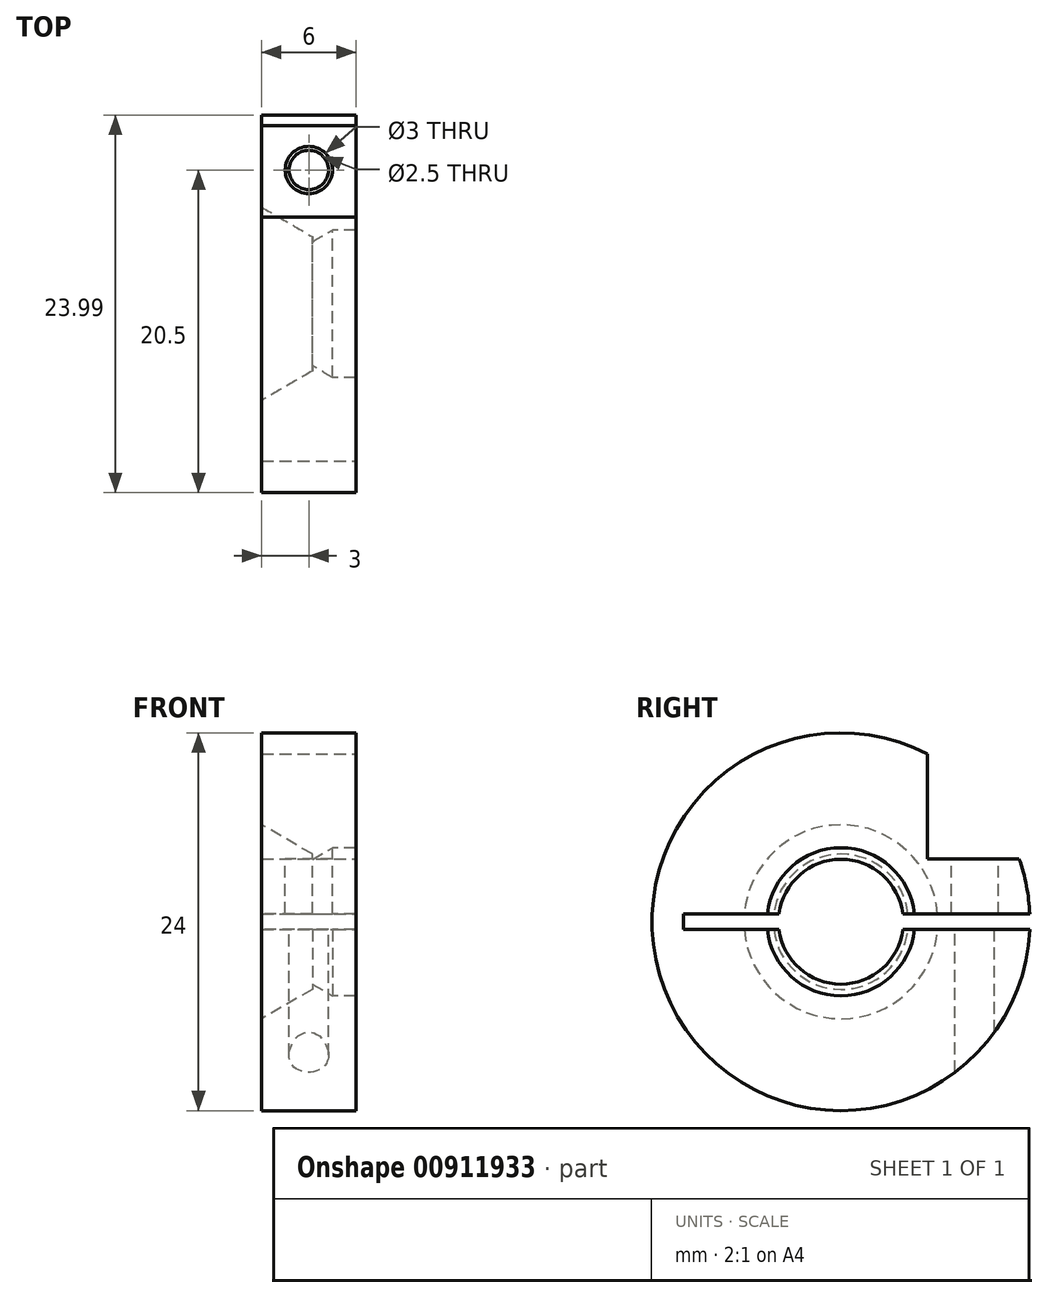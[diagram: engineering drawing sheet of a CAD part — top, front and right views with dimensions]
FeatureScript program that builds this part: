
annotation { "Feature Type Name" : "Feature", "Feature Type Description" : "" }
export const myFeature = defineFeature(function(context is Context, id is Id, definition is map)
    precondition{}
    {
        {
            var Q0;
            Q0=qCreatedBy(makeId("Top.planeOp"),FACE);
            var sketch = newSketch(context, id + "F0", { "sketchPlane" : qUnion([Q0])});
            skCircle(sketch, "E0", {"center": v(0, 8.5) * mm, "radius": 1.5 * mm});
            skCircle(sketch, "E1", {"center": v(0, 8.5) * mm, "radius": 2.8 * mm});
            skLineSegment(sketch, "E2", {"start": v(3, -4.7) * mm, "end": v(3, -12) * mm});
            skLineSegment(sketch, "E3", {"start": v(1.5, -4.7) * mm, "end": v(3, -4.7) * mm});
            skLineSegment(sketch, "E4", {"start": v(1.5, -4.7) * mm, "end": v(0.23, -3.97) * mm});
            skLineSegment(sketch, "E5", {"start": v(-3, -12) * mm, "end": v(3, -12) * mm});
            skLineSegment(sketch, "E6", {"start": v(-3, -6.16) * mm, "end": v(-3, -12) * mm});
            skLineSegment(sketch, "E7", {"start": v(0.23, -4.3) * mm, "end": v(-3, -6.16) * mm});
            skLineSegment(sketch, "E8", {"start": v(0.23, -3.97) * mm, "end": v(0.23, -4.3) * mm});
            skLineSegment(sketch, "E9", {"start": v(1.5, 4.7) * mm, "end": v(3, 4.7) * mm});
            skLineSegment(sketch, "E10", {"start": v(1.5, 4.7) * mm, "end": v(0.23, 3.97) * mm});
            skLineSegment(sketch, "E11", {"start": v(-3, 12) * mm, "end": v(3, 12) * mm});
            skLineSegment(sketch, "E12", {"start": v(0.23, 4.3) * mm, "end": v(-3, 6.16) * mm});
            skLineSegment(sketch, "E13", {"start": v(-3, 6.16) * mm, "end": v(-3, 12) * mm});
            skLineSegment(sketch, "E14", {"start": v(0.23, 3.97) * mm, "end": v(0.23, 4.3) * mm});
            skLineSegment(sketch, "E15", {"start": v(3, 4.7) * mm, "end": v(3, 12) * mm});
            skLineSegment(sketch, "E16", {"start": v(-14.26, 0) * mm, "end": v(18.11, 0) * mm, "construction": true});
            skSolve(sketch);
        }
        {
            var Q0;
            Q0=makeQuery(id+"F0.imprint","IMPRINT",FACE,{"disambiguationData":[TD([[makeQuery(id+"F0.imprint","IMPRINT",EDGE,{"derivedFrom":sQuery(id+"F0.wireOp",EDGE,"E2")}),-1.0]])]});
            var Q1;
            Q1=sQuery(id+"F0.wireOp",EDGE,"E16");
            revolve(context, id + "F1", {"surfaceOperationType" : NewSurfaceOperationType.NEW, "entities" : qUnion([Q0]), "axis" : qUnion([Q1]), "revolveType" : RevolveType.FULL});
        }
        {
            var Q0;
            Q0=makeQuery(id+"F1.opRevolve","SWEPT_FACE",FACE,{"disambiguationData":[OSD([sQuery(id+"F0.wireOp",EDGE,"E2")])]});
            var sketch = newSketch(context, id + "F2", { "sketchPlane" : qUnion([Q0])});
            skLineSegment(sketch, "E17", {"start": v(0, 12) * mm, "end": v(0, 0) * mm, "construction": true});
            skLineSegment(sketch, "E18", {"start": v(0, 0) * mm, "end": v(12, 0) * mm, "construction": true});
            skLineSegment(sketch, "E19", {"start": v(5.5, 10.67) * mm, "end": v(5.5, 4) * mm});
            skLineSegment(sketch, "E20", {"start": v(5.5, 4) * mm, "end": v(11.31, 4) * mm});
            skLineSegment(sketch, "E21", {"start": v(-10, 0.5) * mm, "end": v(13, 0.5) * mm});
            skLineSegment(sketch, "E22", {"start": v(13, 0.5) * mm, "end": v(13, -0.5) * mm});
            skLineSegment(sketch, "E23", {"start": v(13, -0.5) * mm, "end": v(-10, -0.5) * mm});
            skLineSegment(sketch, "E24", {"start": v(-10, -0.5) * mm, "end": v(-10, 0.5) * mm});
            skSolve(sketch);
        }
        {
            var Q0;
            {var subQ0=sQuery(id+"F2.wireOp",EDGE,"E19");Q0=makeQuery(id+"F2.imprint","IMPRINT",FACE,{"disambiguationData":[TD([[makeQuery(id+"F2.imprint","IMPRINT",EDGE,{"derivedFrom":subQ0}),1.0]])]});}
            var Q1;
            {var subQ0=sQuery(id+"F2.wireOp",EDGE,"E21");var subQ1=sQuery(id+"F0.wireOp",EDGE,"E2");var subQ2=makeQuery(id+"F1.opRevolve","SWEPT_EDGE",EDGE,{"disambiguationData":[OSD([subQ1,sQuery(id+"F0.wireOp",EDGE,"E5")])]});var subQ3=makeQuery(id+"F2.imprint","INTERSECT",VERTEX,{"derivedFrom":[subQ2,subQ0]});Q1=makeQuery(id+"F2.imprint","IMPRINT",FACE,{"disambiguationData":[TD([[makeQuery(id+"F2.imprint","IMPRINT",EDGE,{"disambiguationData":[TD([[subQ3,1.0]])],"derivedFrom":subQ0}),-1.0]])]});}
            var Q2;
            {var subQ0=sQuery(id+"F2.wireOp",EDGE,"E24");Q2=makeQuery(id+"F2.imprint","IMPRINT",FACE,{"disambiguationData":[TD([[makeQuery(id+"F2.imprint","IMPRINT",EDGE,{"derivedFrom":subQ0}),-1.0]])]});}
            var Q3;
            {var subQ0=sQuery(id+"F2.wireOp",EDGE,"E21");var subQ1=makeQuery(id+"F1.opRevolve","SWEPT_EDGE",EDGE,{"disambiguationData":[OSD([sQuery(id+"F0.wireOp",EDGE,"E2"),sQuery(id+"F0.wireOp",EDGE,"E3")])]});var subQ2=makeQuery(id+"F2.imprint","INTERSECT",VERTEX,{"disambiguationData":[OD(0.0)],"derivedFrom":[subQ1,subQ0]});Q3=makeQuery(id+"F2.imprint","IMPRINT",FACE,{"disambiguationData":[TD([[makeQuery(id+"F2.imprint","IMPRINT",EDGE,{"disambiguationData":[TD([[subQ2,-1.0]])],"derivedFrom":subQ0}),-1.0]])]});}
            extrude(context, id + "F3", {"entities" : qUnion([Q0, Q1, Q2, Q3]), "operationType" : NewBodyOperationType.REMOVE, "endBound" : BoundingType.THROUGH_ALL, "oppositeDirection" : true, "depth" : 25 * mm, "offsetDistance" : 25 * mm});
        }
        {
            var Q0;
            Q0=makeQuery(id+"F3.boolean.opBoolean","COPY",FACE,{"derivedFrom":makeQuery(id+"F3.opExtrude","SWEPT_FACE",FACE,{"disambiguationData":[OSD([sQuery(id+"F2.wireOp",EDGE,"E20")])]})});
            var sketch = newSketch(context, id + "F4", { "sketchPlane" : qUnion([Q0])});
            skCircle(sketch, "E25", {"center": v(0, 8.5) * mm, "radius": 1.5 * mm});
            skSolve(sketch);
        }
        {
            var Q0;
            Q0=makeQuery(id+"F4.imprint","IMPRINT",FACE,{"disambiguationData":[TD([[makeQuery(id+"F4.imprint","IMPRINT",EDGE,{"derivedFrom":sQuery(id+"F4.wireOp",EDGE,"E25")}),1.0]])]});
            var Q1;
            Q1=makeQuery(id+"F3.boolean.opBoolean","COPY",FACE,{"disambiguationData":[TD([makeQuery(id+"F1.opRevolve","SWEPT_FACE",FACE,{"disambiguationData":[OSD([sQuery(id+"F0.wireOp",EDGE,"E5")])]})])],"derivedFrom":makeQuery(id+"F3.opExtrude","SWEPT_FACE",FACE,{"disambiguationData":[OSD([sQuery(id+"F2.wireOp",EDGE,"E21")])]})});
            extrude(context, id + "F5", {"entities" : qUnion([Q0]), "operationType" : NewBodyOperationType.REMOVE, "endBound" : BoundingType.UP_TO_SURFACE, "oppositeDirection" : true, "depth" : 25 * mm, "endBoundEntityFace" : qUnion([Q1]), "offsetDistance" : 25 * mm});
        }
        {
            var Q0;
            Q0=makeQuery(id+"F3.boolean.opBoolean","COPY",FACE,{"disambiguationData":[TD([makeQuery(id+"F1.opRevolve","SWEPT_FACE",FACE,{"disambiguationData":[OSD([sQuery(id+"F0.wireOp",EDGE,"E5")])]})])],"derivedFrom":makeQuery(id+"F3.opExtrude","SWEPT_FACE",FACE,{"disambiguationData":[OSD([sQuery(id+"F2.wireOp",EDGE,"E23")])]})});
            var sketch = newSketch(context, id + "F6", { "sketchPlane" : qUnion([Q0])});
            skCircle(sketch, "E26", {"center": v(0, 8.5) * mm, "radius": 1.25 * mm});
            skSolve(sketch);
        }
        {
            var Q0;
            Q0=makeQuery(id+"F6.imprint","IMPRINT",FACE,{"disambiguationData":[TD([[makeQuery(id+"F6.imprint","IMPRINT",EDGE,{"derivedFrom":sQuery(id+"F6.wireOp",EDGE,"E26")}),1.0]])]});
            extrude(context, id + "F7", {"entities" : qUnion([Q0]), "operationType" : NewBodyOperationType.REMOVE, "endBound" : BoundingType.THROUGH_ALL, "oppositeDirection" : true, "depth" : 25 * mm, "offsetDistance" : 25 * mm});
        }
    });
